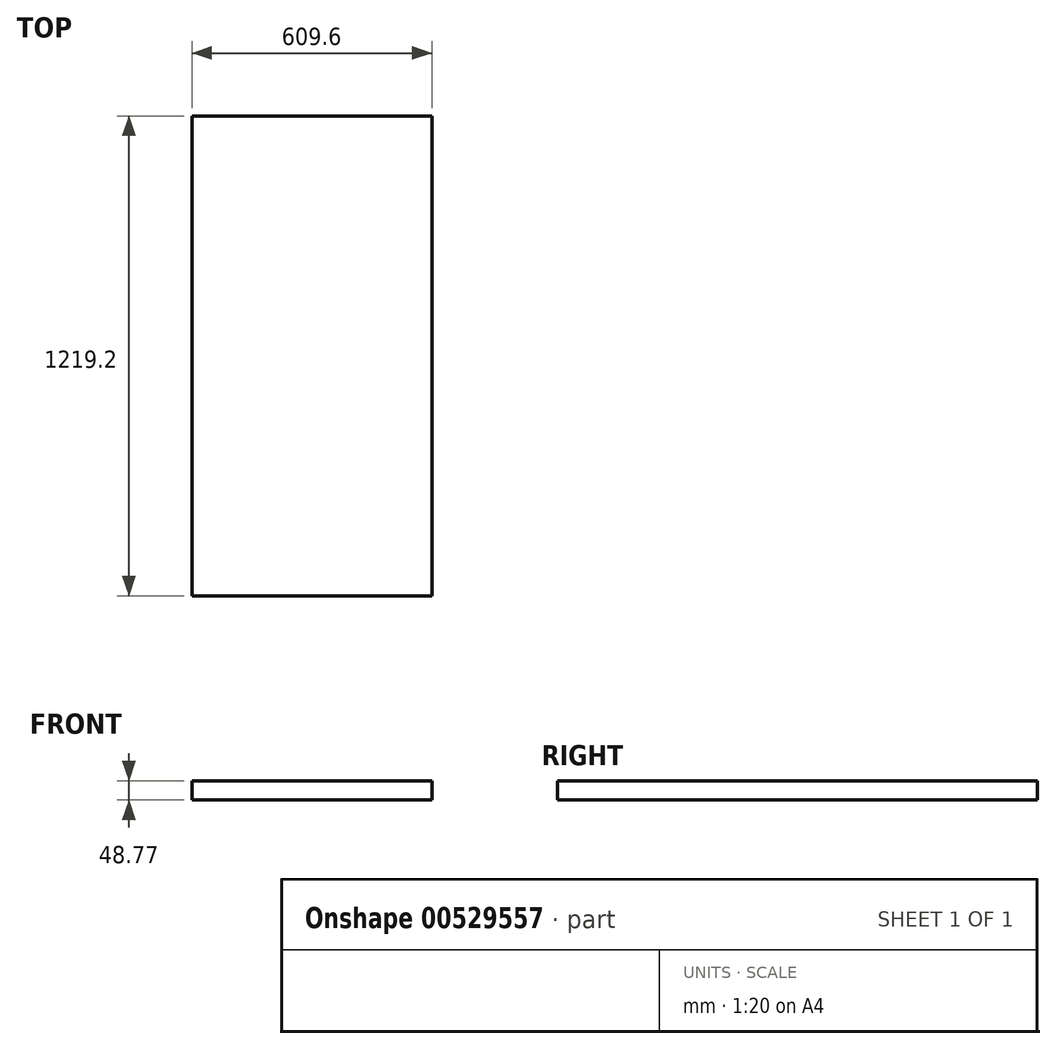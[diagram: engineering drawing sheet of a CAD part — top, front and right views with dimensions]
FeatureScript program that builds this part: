
annotation { "Feature Type Name" : "Feature", "Feature Type Description" : "" }
export const myFeature = defineFeature(function(context is Context, id is Id, definition is map)
    precondition{}
    {
        {
            var Q0;
            Q0=qCreatedBy(makeId("Top.planeOp"),FACE);
            var sketch = newSketch(context, id + "F0", { "sketchPlane" : qUnion([Q0])});
            skLineSegment(sketch, "E0.bottom", {"start": v(-303.1, -724.98) * mm, "end": v(306.5, -724.98) * mm});
            skLineSegment(sketch, "E0.top", {"start": v(-303.1, 494.22) * mm, "end": v(306.5, 494.22) * mm});
            skLineSegment(sketch, "E0.left", {"start": v(-303.1, -724.98) * mm, "end": v(-303.1, 494.22) * mm});
            skLineSegment(sketch, "E0.right", {"start": v(306.5, -724.98) * mm, "end": v(306.5, 494.22) * mm});
            skSolve(sketch);
        }
        {
            var Q0;
            Q0=makeQuery(id+"F0.imprint","IMPRINT",FACE,{"disambiguationData":[TD([[makeQuery(id+"F0.imprint","IMPRINT",EDGE,{"derivedFrom":sQuery(id+"F0.wireOp",EDGE,"E0.bottom")}),1.0]])]});
            extrude(context, id + "F1", {"entities" : qUnion([Q0]), "depth" : 48.77 * mm, "offsetDistance" : 30.48 * mm});
        }
    });
